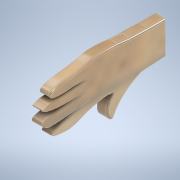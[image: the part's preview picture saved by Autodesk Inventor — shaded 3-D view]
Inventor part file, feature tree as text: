
AUTODESK INVENTOR PART (.ipt)
format: ipt  version: 2021 (Build 250183000, 183)  size: 300,032 bytes
history: native  units: mm
features: fillet x6, extrude x1, chamfer x1, sketch x1
ambient origin geometry x8: Origin, YZ Plane, XZ Plane, XY Plane, X Axis, Y Axis, Z Axis, Center Point
bodies: Solid1 (feature_tree)
feature tree (9):
  extrude  "Extrusion1"  Depth=4.0mm
  fillet  "Fillet1"  Radius=15.187015mm
  fillet  "Fillet2"  Radius=20.0mm
  fillet  "Fillet3"  Radius=6.5mm
  chamfer  "Chamfer1"  Distance=28.0mm
  fillet  "Fillet4"  Radius=25.0mm
  fillet  "Fillet5"  Radius=0.610865mm
  fillet  "Fillet6"  Radius=5.0mm
  sketch  "Sketch1"  dims[d0=6.0mm d1=4.0mm d2=15.187015mm d3=20.0mm d4=6.5mm d5=28.0mm d6=25.0mm d7=0.610865mm d8=5.0mm d9=0.0mm d10=1.0mm d11=1.0mm d12=1.0mm d13=1.0mm d14=2.0mm d15=45.0deg d16=1.0mm d17=1.0mm d18=1.0mm]
